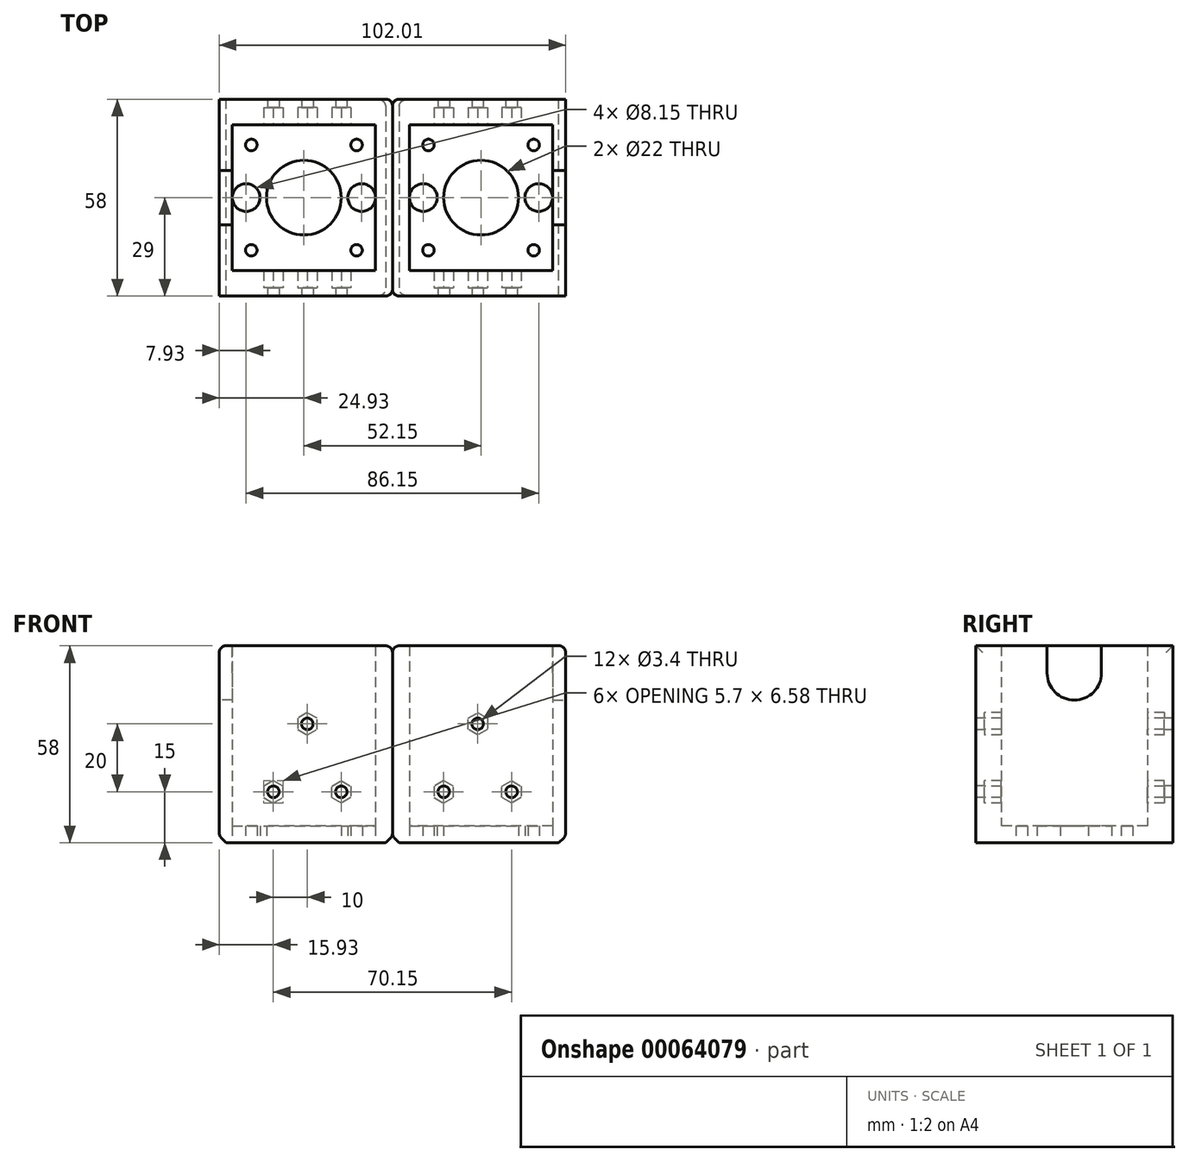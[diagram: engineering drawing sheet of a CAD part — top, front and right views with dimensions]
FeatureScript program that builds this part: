
annotation { "Feature Type Name" : "Feature", "Feature Type Description" : "" }
export const myFeature = defineFeature(function(context is Context, id is Id, definition is map)
    precondition{}
    {
        {
            var Q0;
            Q0=qCreatedBy(makeId("Top.planeOp"),FACE);
            var sketch = newSketch(context, id + "F0", { "sketchPlane" : qUnion([Q0])});
            skCircle(sketch, "E0", {"center": v(0, 0) * mm, "radius": 11 * mm});
            skCircle(sketch, "E1", {"center": v(-17, 0) * mm, "radius": 4.08 * mm});
            skLineSegment(sketch, "E2", {"start": v(0, 0) * mm, "end": v(0, 41.87) * mm, "construction": true});
            skCircle(sketch, "E3.MirrorC", {"center": v(17, 0) * mm, "radius": 4.08 * mm});
            skLineSegment(sketch, "E4.rect.bottom", {"start": v(15.5, -15.5) * mm, "end": v(-15.5, -15.5) * mm, "construction": true});
            skLineSegment(sketch, "E4.rect.top", {"start": v(15.5, 15.5) * mm, "end": v(-15.5, 15.5) * mm, "construction": true});
            skLineSegment(sketch, "E4.rect.left", {"start": v(15.5, -15.5) * mm, "end": v(15.5, 15.5) * mm, "construction": true});
            skLineSegment(sketch, "E4.rect.right", {"start": v(-15.5, -15.5) * mm, "end": v(-15.5, 15.5) * mm, "construction": true});
            skCircle(sketch, "E5", {"center": v(-15.5, 15.5) * mm, "radius": 1.7 * mm});
            skCircle(sketch, "E6", {"center": v(15.5, 15.5) * mm, "radius": 1.7 * mm});
            skCircle(sketch, "E7", {"center": v(-15.5, -15.5) * mm, "radius": 1.7 * mm});
            skCircle(sketch, "E8", {"center": v(15.5, -15.5) * mm, "radius": 1.7 * mm});
            skLineSegment(sketch, "E9.bottom", {"start": v(-24.93, 29) * mm, "end": v(26.07, 29) * mm});
            skLineSegment(sketch, "E9.top", {"start": v(-24.93, -29) * mm, "end": v(26.07, -29) * mm});
            skLineSegment(sketch, "E9.left", {"start": v(-24.93, 29) * mm, "end": v(-24.93, -29) * mm});
            skLineSegment(sketch, "E9.right", {"start": v(26.08, 29) * mm, "end": v(26.07, -29) * mm});
            skLineSegment(sketch, "E10", {"start": v(-24.93, 0) * mm, "end": v(26.07, 0) * mm, "construction": true});
            skLineSegment(sketch, "E11.bottom", {"start": v(-21.08, 21.5) * mm, "end": v(21.08, 21.5) * mm});
            skLineSegment(sketch, "E11.top", {"start": v(-21.08, -21.5) * mm, "end": v(21.08, -21.5) * mm});
            skLineSegment(sketch, "E11.left", {"start": v(-21.08, 21.5) * mm, "end": v(-21.07, -21.5) * mm});
            skLineSegment(sketch, "E11.right", {"start": v(21.08, 21.5) * mm, "end": v(21.08, -21.5) * mm});
            skPoint(sketch, "E12", {"position": v(0, 15.5) * mm});
            skSolve(sketch);
        }
        {
            var Q0;
            Q0 = qSketchRegion(id + "F0", true);
            extrude(context, id + "F1", {"entities" : qUnion([Q0]), "depth" : 58 * mm});
        }
        {
            var Q0;
            Q0=makeQuery(id+"F0.imprint","IMPRINT",FACE,{"disambiguationData":[TD([[makeQuery(id+"F0.imprint","IMPRINT",EDGE,{"derivedFrom":sQuery(id+"F0.wireOp",EDGE,"E0")}),-1.0]])]});
            var Q1;
            Q1=makeQuery(id+"F0.imprint","IMPRINT",FACE,{"disambiguationData":[TD([[makeQuery(id+"F0.imprint","IMPRINT",EDGE,{"derivedFrom":sQuery(id+"F0.wireOp",EDGE,"E9.bottom")}),-1.0]])]});
            extrude(context, id + "F2", {"entities" : qUnion([Q0, Q1]), "operationType" : NewBodyOperationType.ADD, "depth" : 5 * mm});
        }
        {
            var Q0;
            Q0=qCreatedBy(makeId("Front.planeOp"),FACE);
            var sketch = newSketch(context, id + "F3", { "sketchPlane" : qUnion([Q0])});
            skCircle(sketch, "E13.cCircle", {"center": v(-9, 15) * mm, "radius": 2.85 * mm, "construction": true});
            skLineSegment(sketch, "E13.0", {"start": v(-6.15, 16.65) * mm, "end": v(-6.15, 13.35) * mm});
            skLineSegment(sketch, "E13.1", {"start": v(-6.15, 13.35) * mm, "end": v(-9, 11.7) * mm});
            skLineSegment(sketch, "E13.2", {"start": v(-9, 11.7) * mm, "end": v(-11.85, 13.35) * mm});
            skLineSegment(sketch, "E13.3", {"start": v(-11.85, 13.35) * mm, "end": v(-11.85, 16.65) * mm});
            skLineSegment(sketch, "E13.4", {"start": v(-11.85, 16.65) * mm, "end": v(-9, 18.3) * mm});
            skLineSegment(sketch, "E13.5", {"start": v(-9, 18.3) * mm, "end": v(-6.15, 16.65) * mm});
            skPoint(sketch, "E13.0.midPoint", {"position": v(-6.15, 15) * mm});
            skLineSegment(sketch, "E14", {"start": v(0, 0) * mm, "end": v(0, 58) * mm, "construction": true});
            skLineSegment(sketch, "E15.bottom", {"start": v(-9, 35) * mm, "end": v(11, 35) * mm, "construction": true});
            skLineSegment(sketch, "E15.top", {"start": v(-9, 15) * mm, "end": v(11, 15) * mm, "construction": true});
            skLineSegment(sketch, "E15.left", {"start": v(-9, 35) * mm, "end": v(-9, 15) * mm, "construction": true});
            skLineSegment(sketch, "E15.right", {"start": v(11, 35) * mm, "end": v(11, 15) * mm, "construction": true});
            skLineSegment(sketch, "E16", {"start": v(1, 35) * mm, "end": v(1, 15) * mm, "construction": true});
            skLineSegment(sketch, "E17.MirrorCS", {"start": v(8.15, 16.65) * mm, "end": v(8.15, 13.35) * mm});
            skCircle(sketch, "E18.MirrorC", {"center": v(11, 15) * mm, "radius": 2.85 * mm, "construction": true});
            skLineSegment(sketch, "E19.MirrorCS", {"start": v(8.15, 13.35) * mm, "end": v(11, 11.7) * mm});
            skLineSegment(sketch, "E20.MirrorCS", {"start": v(11, 11.7) * mm, "end": v(13.85, 13.35) * mm});
            skLineSegment(sketch, "E21.MirrorCS", {"start": v(13.85, 16.65) * mm, "end": v(11, 18.3) * mm});
            skPoint(sketch, "E22.MirrorP", {"position": v(8.15, 15) * mm});
            skLineSegment(sketch, "E23.MirrorCS", {"start": v(11, 18.3) * mm, "end": v(8.15, 16.65) * mm});
            skLineSegment(sketch, "E24.MirrorCS", {"start": v(13.85, 13.35) * mm, "end": v(13.85, 16.65) * mm});
            skCircle(sketch, "E25.cCircle", {"center": v(1, 35) * mm, "radius": 2.85 * mm, "construction": true});
            skLineSegment(sketch, "E25.0", {"start": v(-1.85, 33.35) * mm, "end": v(-1.85, 36.65) * mm});
            skLineSegment(sketch, "E25.1", {"start": v(-1.85, 36.65) * mm, "end": v(1, 38.3) * mm});
            skLineSegment(sketch, "E25.2", {"start": v(1, 38.3) * mm, "end": v(3.85, 36.65) * mm});
            skLineSegment(sketch, "E25.3", {"start": v(3.85, 36.65) * mm, "end": v(3.85, 33.35) * mm});
            skLineSegment(sketch, "E25.4", {"start": v(3.85, 33.35) * mm, "end": v(1, 31.7) * mm});
            skLineSegment(sketch, "E25.5", {"start": v(1, 31.7) * mm, "end": v(-1.85, 33.35) * mm});
            skPoint(sketch, "E25.0.midPoint", {"position": v(-1.85, 35) * mm});
            skCircle(sketch, "E26", {"center": v(-9, 15) * mm, "radius": 1.7 * mm});
            skCircle(sketch, "E27", {"center": v(11, 15) * mm, "radius": 1.7 * mm});
            skCircle(sketch, "E28", {"center": v(1, 35) * mm, "radius": 1.7 * mm});
            skSolve(sketch);
        }
        {
            var Q0;
            Q0=makeQuery(id+"F3.imprint","IMPRINT",FACE,{"disambiguationData":[TD([[makeQuery(id+"F3.imprint","IMPRINT",EDGE,{"derivedFrom":sQuery(id+"F3.wireOp",EDGE,"E28")}),1.0]])]});
            var Q1;
            Q1=makeQuery(id+"F3.imprint","IMPRINT",FACE,{"disambiguationData":[TD([[makeQuery(id+"F3.imprint","IMPRINT",EDGE,{"derivedFrom":sQuery(id+"F3.wireOp",EDGE,"E27")}),1.0]])]});
            var Q2;
            Q2=makeQuery(id+"F3.imprint","IMPRINT",FACE,{"disambiguationData":[TD([[makeQuery(id+"F3.imprint","IMPRINT",EDGE,{"derivedFrom":sQuery(id+"F3.wireOp",EDGE,"E26")}),1.0]])]});
            extrude(context, id + "F4", {"entities" : qUnion([Q0, Q1, Q2]), "operationType" : NewBodyOperationType.REMOVE, "endBound" : BoundingType.SYMMETRIC, "oppositeDirection" : true, "depth" : 199 * mm});
        }
        {
            var Q0;
            Q0=makeQuery(id+"F3.imprint","IMPRINT",FACE,{"disambiguationData":[TD([[makeQuery(id+"F3.imprint","IMPRINT",EDGE,{"derivedFrom":sQuery(id+"F3.wireOp",EDGE,"E25.0")}),-1.0]])]});
            var Q1;
            Q1=makeQuery(id+"F3.imprint","IMPRINT",FACE,{"disambiguationData":[TD([[makeQuery(id+"F3.imprint","IMPRINT",EDGE,{"derivedFrom":sQuery(id+"F3.wireOp",EDGE,"E17.MirrorCS")}),1.0]])]});
            var Q2;
            Q2=makeQuery(id+"F3.imprint","IMPRINT",FACE,{"disambiguationData":[TD([[makeQuery(id+"F3.imprint","IMPRINT",EDGE,{"derivedFrom":sQuery(id+"F3.wireOp",EDGE,"E13.0")}),-1.0]])]});
            extrude(context, id + "F5", {"entities" : qUnion([Q0, Q1, Q2]), "operationType" : NewBodyOperationType.REMOVE, "endBound" : BoundingType.SYMMETRIC, "oppositeDirection" : true, "depth" : (43 + 5 * 2) * mm});
        }
        {
            var Q0;
            Q0=makeQuery(id+"F1.opExtrude","SWEPT_FACE",FACE,{"disambiguationData":[OSD([sQuery(id+"F0.wireOp",EDGE,"E9.left")])]});
            var sketch = newSketch(context, id + "F6", { "sketchPlane" : qUnion([Q0])});
            skLineSegment(sketch, "E29.rect.bottom", {"start": v(8, 50) * mm, "end": v(-8, 50) * mm, "construction": true});
            skLineSegment(sketch, "E29.rect.top", {"start": v(8, 66) * mm, "end": v(-8, 66) * mm});
            skLineSegment(sketch, "E29.rect.left", {"start": v(8, 50) * mm, "end": v(8, 66) * mm});
            skLineSegment(sketch, "E29.rect.right", {"start": v(-8, 50) * mm, "end": v(-8, 66) * mm});
            skPoint(sketch, "E29.rect.middle", {"position": v(0, 58) * mm});
            skArc(sketch, "E30", {"start": v(-8, 50) * mm, "mid": v(0, 42) * mm, "end": v(8, 50) * mm});
            skSolve(sketch);
        }
        {
            var Q0;
            {var subQ0=sQuery(id+"F6.wireOp",EDGE,"E30");Q0=makeQuery(id+"F6.imprint","IMPRINT",FACE,{"disambiguationData":[TD([[makeQuery(id+"F6.imprint","IMPRINT",EDGE,{"derivedFrom":subQ0}),1.0]])]});}
            var Q1;
            Q1=sQuery(id+"F6.wireOp",EDGE,"E29.rect.bottom");
            var Q2;
            Q2=makeQuery(id+"F1.opExtrude","SWEPT_FACE",FACE,{"disambiguationData":[OSD([sQuery(id+"F0.wireOp",EDGE,"E11.left")])]});
            extrude(context, id + "F7", {"entities" : qUnion([Q0]), "operationType" : NewBodyOperationType.REMOVE, "surfaceEntities" : qUnion([Q1]), "endBound" : BoundingType.UP_TO_SURFACE, "oppositeDirection" : true, "endBoundEntityFace" : qUnion([Q2]), "depth" : 25 * mm});
        }
        {
            var Q0;
            Q0=makeQuery(id+"F1.opExtrude","CAP_EDGE",EDGE,{"disambiguationData":[OSD([sQuery(id+"F0.wireOp",EDGE,"E9.left")])],"isStart":true});
            var Q1;
            Q1=makeQuery(id+"F1.opExtrude","CAP_EDGE",EDGE,{"disambiguationData":[OSD([sQuery(id+"F0.wireOp",EDGE,"E9.right")])],"isStart":true});
            chamfer(context, id + "F8", {"entities" : qUnion([Q0, Q1]), "width" : 2 * mm, "tangentPropagation" : true});
        }
        {
            var Q0;
            {var subQ0=sQuery(id+"F0.wireOp",EDGE,"E9.bottom");Q0=makeQuery(id+"F8.opChamfer","BLEND_EDGE",EDGE,{"blendedFrom":[makeQuery(id+"F1.opExtrude","CAP_EDGE",EDGE,{"disambiguationData":[OSD([subQ0])],"isStart":true}),makeQuery(id+"F1.opExtrude","SWEPT_FACE",FACE,{"disambiguationData":[OSD([subQ0])]})],"blendedInto":[makeQuery(id+"F1.opExtrude","SWEPT_FACE",FACE,{"disambiguationData":[OSD([subQ0])]})]});}
            var Q1;
            {var subQ0=sQuery(id+"F0.wireOp",EDGE,"E9.right");Q1=makeQuery(id+"F8.opChamfer","BLEND_EDGE",EDGE,{"blendedFrom":[makeQuery(id+"F1.opExtrude","CAP_EDGE",EDGE,{"disambiguationData":[OSD([subQ0])],"isStart":true}),makeQuery(id+"F1.opExtrude","SWEPT_FACE",FACE,{"disambiguationData":[OSD([subQ0])]})],"blendedInto":[makeQuery(id+"F1.opExtrude","SWEPT_FACE",FACE,{"disambiguationData":[OSD([subQ0])]})]});}
            var Q2;
            {var subQ0=sQuery(id+"F0.wireOp",EDGE,"E9.top");Q2=makeQuery(id+"F8.opChamfer","BLEND_EDGE",EDGE,{"blendedFrom":[makeQuery(id+"F1.opExtrude","CAP_EDGE",EDGE,{"disambiguationData":[OSD([subQ0])],"isStart":true}),makeQuery(id+"F1.opExtrude","SWEPT_FACE",FACE,{"disambiguationData":[OSD([subQ0])]})],"blendedInto":[makeQuery(id+"F1.opExtrude","SWEPT_FACE",FACE,{"disambiguationData":[OSD([subQ0])]})]});}
            var Q3;
            {var subQ0=sQuery(id+"F0.wireOp",EDGE,"E9.left");Q3=makeQuery(id+"F8.opChamfer","BLEND_EDGE",EDGE,{"blendedFrom":[makeQuery(id+"F1.opExtrude","CAP_EDGE",EDGE,{"disambiguationData":[OSD([subQ0])],"isStart":true}),makeQuery(id+"F1.opExtrude","SWEPT_FACE",FACE,{"disambiguationData":[OSD([subQ0])]})],"blendedInto":[makeQuery(id+"F1.opExtrude","SWEPT_FACE",FACE,{"disambiguationData":[OSD([subQ0])]})]});}
            fillet(context, id + "F9", {"entities" : qUnion([Q0, Q1, Q2, Q3]), "radius" : 2 * mm, "tangentPropagation" : true, "allowEdgeOverflow" : false});
        }
        {
            var Q0;
            Q0=makeQuery(id+"F1.opExtrude","SWEPT_EDGE",EDGE,{"disambiguationData":[OSD([sQuery(id+"F0.wireOp",EDGE,"E9.bottom"),sQuery(id+"F0.wireOp",EDGE,"E9.right")])]});
            var Q1;
            Q1=makeQuery(id+"F1.opExtrude","SWEPT_EDGE",EDGE,{"disambiguationData":[OSD([sQuery(id+"F0.wireOp",EDGE,"E9.top"),sQuery(id+"F0.wireOp",EDGE,"E9.right")])]});
            var Q2;
            {var subQ0=sQuery(id+"F0.wireOp",EDGE,"E9.bottom");var subQ1=sQuery(id+"F0.wireOp",EDGE,"E9.left");Q2=makeQuery(id+"F7.boolean.opBoolean","SPLIT",EDGE,{"disambiguationData":[TD([makeQuery(id+"F1.opExtrude","SWEPT_FACE",FACE,{"disambiguationData":[OSD([subQ0])]})])],"derivedFrom":makeQuery(id+"F1.opExtrude","CAP_EDGE",EDGE,{"disambiguationData":[OSD([subQ1])],"isStart":false})});}
            var Q3;
            {var subQ0=sQuery(id+"F0.wireOp",EDGE,"E9.left");var subQ1=sQuery(id+"F0.wireOp",EDGE,"E9.top");Q3=makeQuery(id+"F7.boolean.opBoolean","SPLIT",EDGE,{"disambiguationData":[TD([makeQuery(id+"F1.opExtrude","SWEPT_FACE",FACE,{"disambiguationData":[OSD([subQ1])]})])],"derivedFrom":makeQuery(id+"F1.opExtrude","CAP_EDGE",EDGE,{"disambiguationData":[OSD([subQ0])],"isStart":false})});}
            var Q4;
            Q4=makeQuery(id+"F1.opExtrude","CAP_EDGE",EDGE,{"disambiguationData":[OSD([sQuery(id+"F0.wireOp",EDGE,"E9.right")])],"isStart":false});
            fillet(context, id + "F10", {"entities" : qUnion([Q0, Q1, Q2, Q3, Q4]), "radius" : 2 * mm, "tangentPropagation" : true, "allowEdgeOverflow" : false});
        }
        {
            var Q0;
            Q0=makeQuery(id+"F1.opExtrude","SWEPT_BODY",BODY,{"disambiguationData":[OSD([sQuery(id+"F0.wireOp",EDGE,"E9.bottom"),sQuery(id+"F0.wireOp",EDGE,"E9.top"),sQuery(id+"F0.wireOp",EDGE,"E9.left"),sQuery(id+"F0.wireOp",EDGE,"E9.right"),sQuery(id+"F0.wireOp",EDGE,"E11.bottom"),sQuery(id+"F0.wireOp",EDGE,"E11.top"),sQuery(id+"F0.wireOp",EDGE,"E11.left"),sQuery(id+"F0.wireOp",EDGE,"E11.right")])]});
            var Q1;
            Q1=makeQuery(id+"F1.opExtrude","SWEPT_FACE",FACE,{"disambiguationData":[OSD([sQuery(id+"F0.wireOp",EDGE,"E9.right")])]});
            mirror(context, id + "F11", {"entities" : qUnion([Q0]), "mirrorPlane" : qUnion([Q1])});
        }
    });
